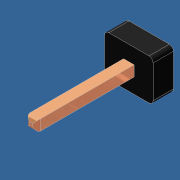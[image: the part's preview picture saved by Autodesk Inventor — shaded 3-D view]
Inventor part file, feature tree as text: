
AUTODESK INVENTOR PART (.ipt)
format: ipt  version: 2012 (Build 160160000, 160)  size: 100,864 bytes
history: native  units: in
note: dims shown in document units (in); Inventor stores cm internally (conversion verified against a paired STEP export)
features: extrude x2, fillet x2, sketch x2
ambient origin geometry x8: Origin, YZ Plane, XZ Plane, XY Plane, X Axis, Y Axis, Z Axis, Center Point
bodies: Solid1 (feature_tree)
feature tree (6):
  extrude  "Extrusion1"  Depth=0.1in
  extrude  "Extrusion2"  Depth=0.013in
  fillet  "Fillet1"  Radius=0.013in
  fillet  "Fillet2"  Radius=0.013in
  sketch  "Sketch1"  dims[d0=0.119in d1=0.1in]
  sketch  "Sketch2"  dims[d2=0.05in d3=0.0in d6=0.013in d7=0.013in d8=0.013in d9=0.013in d10=0.24in d11=0.0in d12=0.01in d13=0.01in]
